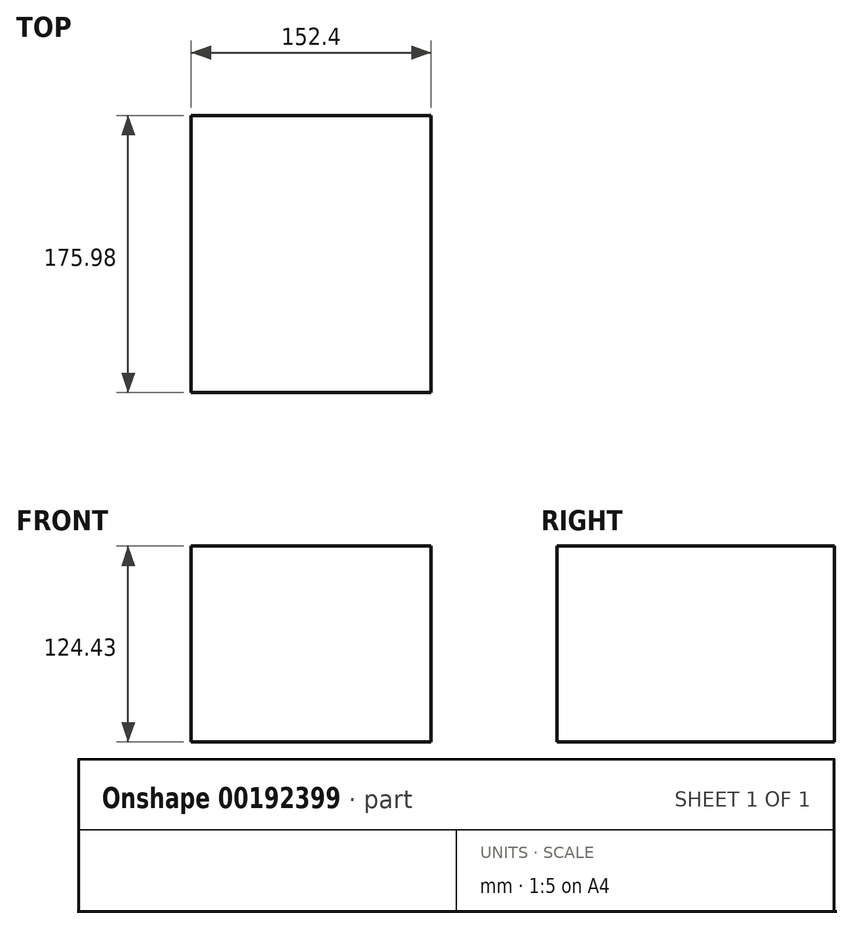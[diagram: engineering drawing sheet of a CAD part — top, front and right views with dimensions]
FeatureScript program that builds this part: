
annotation { "Feature Type Name" : "Feature", "Feature Type Description" : "" }
export const myFeature = defineFeature(function(context is Context, id is Id, definition is map)
    precondition{}
    {
        {
            var Q0;
            Q0=qCreatedBy(makeId("Top.planeOp"),FACE);
            var sketch = newSketch(context, id + "F0", { "sketchPlane" : qUnion([Q0])});
            skCircle(sketch, "E0.cCircle", {"center": v(0, 0) * mm, "radius": 44 * mm, "construction": true});
            skLineSegment(sketch, "E0.0", {"start": v(-76.2, 44) * mm, "end": v(76.2, 44) * mm, "construction": true});
            skLineSegment(sketch, "E0.1", {"start": v(76.2, 44) * mm, "end": v(0, -87.99) * mm, "construction": true});
            skLineSegment(sketch, "E0.2", {"start": v(0, -87.99) * mm, "end": v(-76.2, 44) * mm, "construction": true});
            skPoint(sketch, "E0.0.midPoint", {"position": v(0, 44) * mm});
            skLineSegment(sketch, "E1.bottom", {"start": v(76.2, -87.99) * mm, "end": v(-76.2, -87.99) * mm});
            skLineSegment(sketch, "E1.top", {"start": v(76.2, 87.99) * mm, "end": v(-76.2, 87.99) * mm});
            skLineSegment(sketch, "E1.left", {"start": v(76.2, -87.99) * mm, "end": v(76.2, 87.99) * mm});
            skLineSegment(sketch, "E1.right", {"start": v(-76.2, -87.99) * mm, "end": v(-76.2, 87.99) * mm});
            skSolve(sketch);
        }
        {
            var Q0;
            Q0=qCreatedBy(makeId("Right.planeOp"),FACE);
            var sketch = newSketch(context, id + "F1", { "sketchPlane" : qUnion([Q0])});
            skLineSegment(sketch, "E2", {"start": v(0, 0) * mm, "end": v(0, 124.43) * mm});
            skLineSegment(sketch, "E3", {"start": v(0, 0) * mm, "end": v(-87.99, 0) * mm});
            skLineSegment(sketch, "E4", {"start": v(-87.99, 0) * mm, "end": v(0, 124.43) * mm});
            skLineSegment(sketch, "E5", {"start": v(0, 124.43) * mm, "end": v(44, 0) * mm});
            skSolve(sketch);
        }
        {
            var Q0;
            Q0 = qSketchRegion(id + "F0", true);
            var Q1;
            Q1=sQuery(id+"F1.wireOp",VERTEX,"E5.start");
            extrude(context, id + "F2", {"entities" : qUnion([Q0]), "endBound" : BoundingType.UP_TO_VERTEX, "endBoundEntityVertex" : qUnion([Q1]), "depth" : 25.4 * mm});
        }
    });
